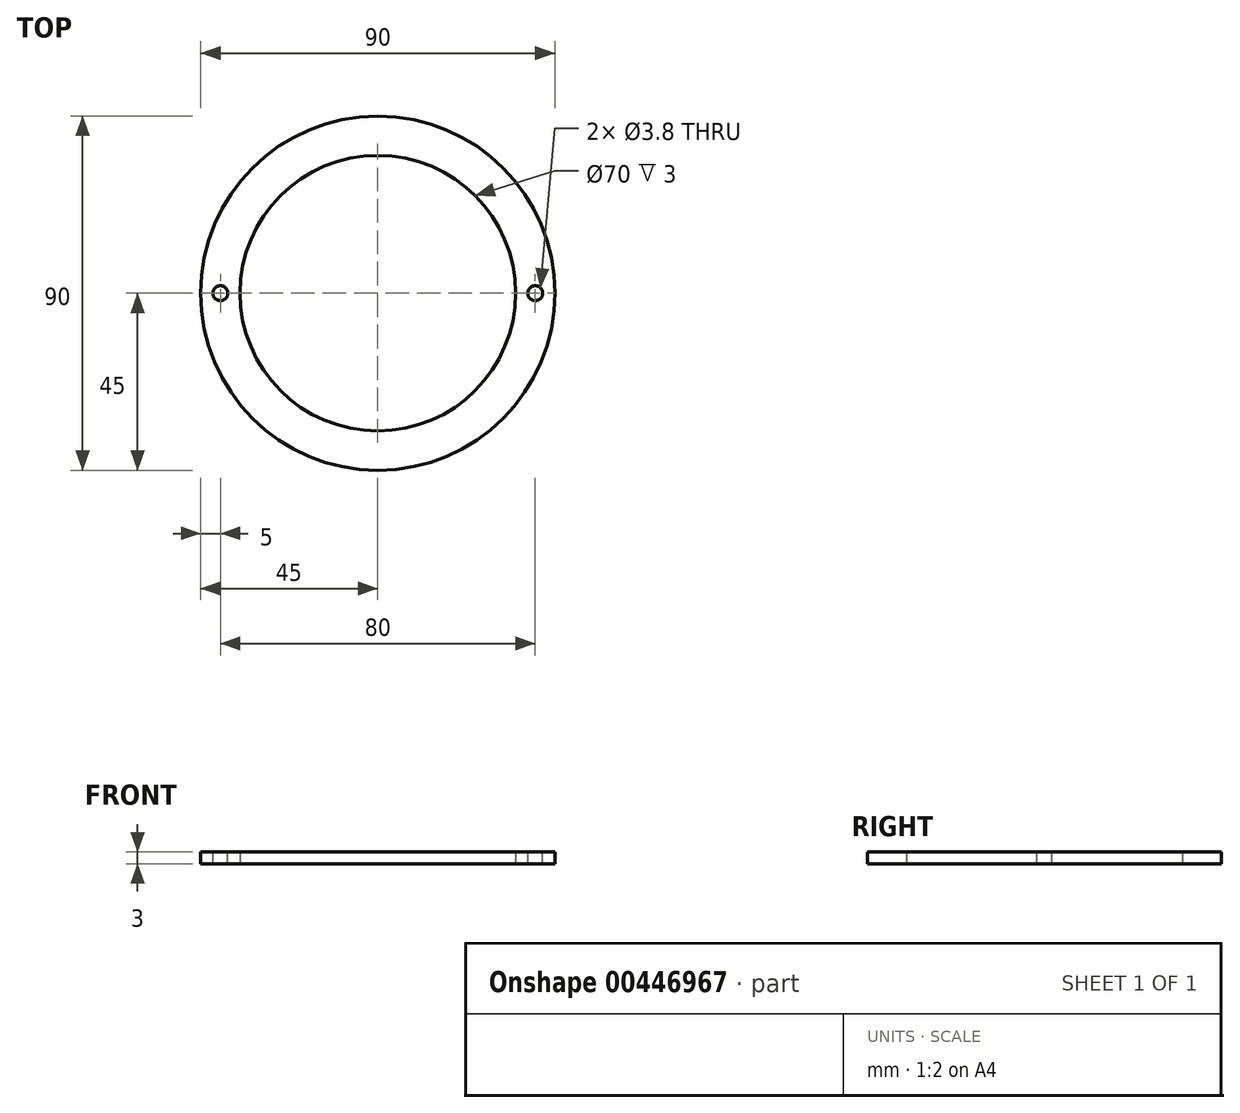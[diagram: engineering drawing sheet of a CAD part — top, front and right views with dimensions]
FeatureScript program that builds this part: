
annotation { "Feature Type Name" : "Feature", "Feature Type Description" : "" }
export const myFeature = defineFeature(function(context is Context, id is Id, definition is map)
    precondition{}
    {
        {
            var Q0;
            Q0=qCreatedBy(makeId("Top.planeOp"),FACE);
            var sketch = newSketch(context, id + "F0", { "sketchPlane" : qUnion([Q0])});
            skCircle(sketch, "E0", {"center": v(0, 0) * mm, "radius": 35 * mm});
            skCircle(sketch, "E1", {"center": v(0, 0) * mm, "radius": 45 * mm});
            skSolve(sketch);
        }
        {
            var Q0;
            Q0=makeQuery(id+"F0.imprint","IMPRINT",FACE,{"disambiguationData":[TD([[makeQuery(id+"F0.imprint","IMPRINT",EDGE,{"derivedFrom":sQuery(id+"F0.wireOp",EDGE,"E0")}),-1.0]])]});
            extrude(context, id + "F1", {"entities" : qUnion([Q0]), "depth" : 3 * mm});
        }
        {
            var Q0;
            Q0=makeQuery(id+"F1.opExtrude","CAP_FACE",FACE,{"disambiguationData":[OSD([sQuery(id+"F0.wireOp",EDGE,"E0"),sQuery(id+"F0.wireOp",EDGE,"E1")])],"isStart":false});
            var sketch = newSketch(context, id + "F2", { "sketchPlane" : qUnion([Q0])});
            skLineSegment(sketch, "E2", {"start": v(0, 0) * mm, "end": v(-40, 0) * mm, "construction": true});
            skCircle(sketch, "E3", {"center": v(-40, 0) * mm, "radius": 1.9 * mm});
            skLineSegment(sketch, "E4", {"start": v(0, 0) * mm, "end": v(0, 8.63) * mm, "construction": true});
            skCircle(sketch, "E5.MirrorC", {"center": v(40, 0) * mm, "radius": 1.9 * mm});
            skSolve(sketch);
        }
        {
            var Q0;
            Q0 = qSketchRegion(id + "F2", true);
            extrude(context, id + "F3", {"entities" : qUnion([Q0]), "operationType" : NewBodyOperationType.REMOVE, "oppositeDirection" : true, "depth" : 25 * mm});
        }
        {
            var Q0;
            Q0=makeQuery(id+"F1.opExtrude","CAP_FACE",FACE,{"disambiguationData":[OSD([sQuery(id+"F0.wireOp",EDGE,"E0"),sQuery(id+"F0.wireOp",EDGE,"E1")])],"isStart":false});
            var sketch = newSketch(context, id + "F4", { "sketchPlane" : qUnion([Q0])});
            skLineSegment(sketch, "E6.bottom", {"start": v(0, -45) * mm, "end": v(55.17, -45) * mm});
            skLineSegment(sketch, "E6.top", {"start": v(0, 52.55) * mm, "end": v(55.17, 52.55) * mm});
            skLineSegment(sketch, "E6.left", {"start": v(0, -45) * mm, "end": v(0, 52.55) * mm});
            skLineSegment(sketch, "E6.right", {"start": v(55.17, -45) * mm, "end": v(55.17, 52.55) * mm});
            skSolve(sketch);
        }
        {
            var Q0;
            Q0 = qSketchRegion(id + "F4", true);
            extrude(context, id + "F5", {"entities" : qUnion([Q0]), "operationType" : NewBodyOperationType.REMOVE, "oppositeDirection" : true, "depth" : 25 * mm});
        }
        {
            var Q0;
            Q0=makeQuery(id+"F1.opExtrude","SWEPT_BODY",BODY,{"disambiguationData":[OSD([sQuery(id+"F0.wireOp",EDGE,"E0"),sQuery(id+"F0.wireOp",EDGE,"E1")])]});
            var Q1;
            Q1=makeQuery(id+"F5.boolean.opBoolean","COPY",FACE,{"disambiguationData":[OD(1.0)],"derivedFrom":makeQuery(id+"F5.opExtrude","SWEPT_FACE",FACE,{"disambiguationData":[OSD([sQuery(id+"F4.wireOp",EDGE,"E6.left")])]})});
            mirror(context, id + "F6", {"operationType" : NewBodyOperationType.ADD, "entities" : qUnion([Q0]), "mirrorPlane" : qUnion([Q1])});
        }
    });
